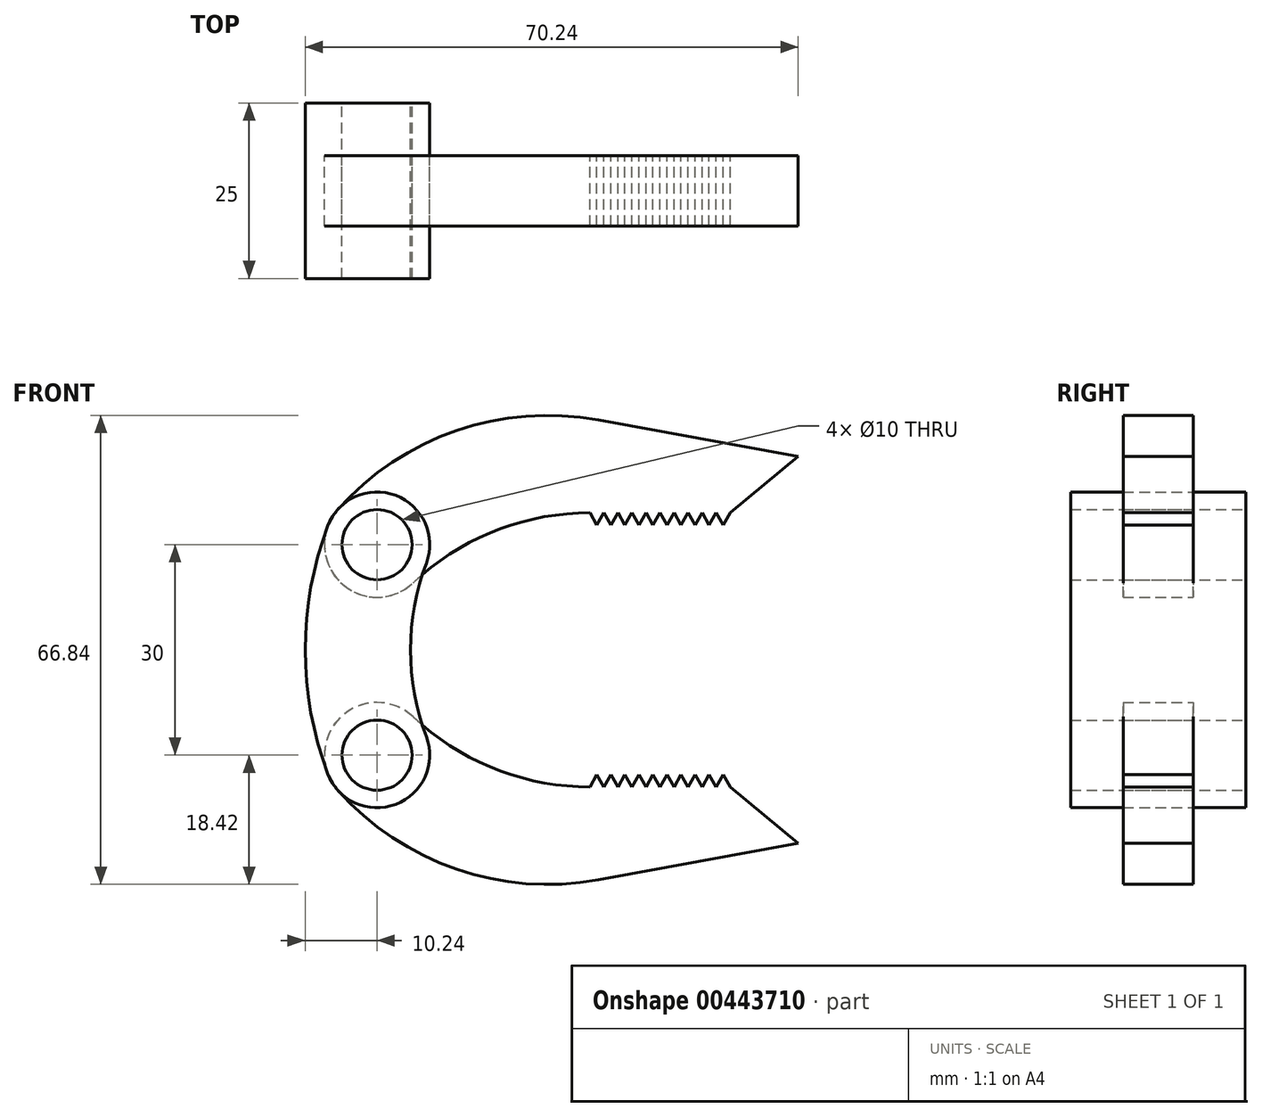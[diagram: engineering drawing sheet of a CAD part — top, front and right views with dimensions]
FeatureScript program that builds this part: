
annotation { "Feature Type Name" : "Feature", "Feature Type Description" : "" }
export const myFeature = defineFeature(function(context is Context, id is Id, definition is map)
    precondition{}
    {
        {
            var Q0;
            Q0=qCreatedBy(makeId("Front.planeOp"),FACE);
            var sketch = newSketch(context, id + "F0", { "sketchPlane" : qUnion([Q0])});
            skLineSegment(sketch, "E0", {"start": v(0, 15) * mm, "end": v(0, -15) * mm, "construction": true});
            skLineSegment(sketch, "E1", {"start": v(0, 0) * mm, "end": v(80, 0) * mm, "construction": true});
            skCircle(sketch, "E2", {"center": v(0, 15) * mm, "radius": 5 * mm});
            skCircle(sketch, "E3", {"center": v(0, -15) * mm, "radius": 5 * mm});
            skArc(sketch, "E4.0", {"start": v(7.02, 12.35) * mm, "mid": v(2.65, 22.02) * mm, "end": v(-7.02, 17.65) * mm});
            skArc(sketch, "E5.0", {"start": v(-7.02, -17.65) * mm, "mid": v(2.65, -22.02) * mm, "end": v(7.02, -12.35) * mm});
            skArc(sketch, "E6", {"start": v(-7.02, 17.65) * mm, "mid": v(-10.24, 0) * mm, "end": v(-7.02, -17.65) * mm});
            skArc(sketch, "E7", {"start": v(7.02, 12.35) * mm, "mid": v(4.76, 0) * mm, "end": v(7.02, -12.35) * mm});
            skSolve(sketch);
        }
        {
            var Q0;
            Q0=qCreatedBy(makeId("Front.planeOp"),FACE);
            var sketch = newSketch(context, id + "F1", { "sketchPlane" : qUnion([Q0])});
            skCircle(sketch, "E8.0", {"center": v(0, 15) * mm, "radius": 5 * mm});
            skArc(sketch, "E9", {"start": v(-5.6, 19.98) * mm, "mid": v(-5.22, 9.62) * mm, "end": v(5.14, 9.54) * mm});
            skCircle(sketch, "E10.0", {"center": v(0, -15) * mm, "radius": 5 * mm});
            skArc(sketch, "E11", {"start": v(5.14, -9.54) * mm, "mid": v(-5.22, -9.62) * mm, "end": v(-5.6, -19.98) * mm});
            skArc(sketch, "E12", {"start": v(31.53, 32.77) * mm, "mid": v(11.28, 31.25) * mm, "end": v(-5.6, 19.98) * mm});
            skLineSegment(sketch, "E13", {"start": v(31.53, 32.77) * mm, "end": v(60, 27.54) * mm});
            skLineSegment(sketch, "E14", {"start": v(60, 27.54) * mm, "end": v(50.33, 19.54) * mm});
            skArc(sketch, "E15", {"start": v(30.33, 19.54) * mm, "mid": v(16.78, 16.95) * mm, "end": v(5.14, 9.54) * mm});
            skLineSegment(sketch, "E16", {"start": v(19.1, 0) * mm, "end": v(64.22, 0) * mm});
            skLineSegment(sketch, "E17.MirrorCS", {"start": v(60, -27.54) * mm, "end": v(50.33, -19.54) * mm});
            skLineSegment(sketch, "E18.MirrorCS", {"start": v(31.53, -32.77) * mm, "end": v(60, -27.54) * mm});
            skArc(sketch, "E19.MirrorCS", {"start": v(30.33, -19.54) * mm, "mid": v(16.78, -16.95) * mm, "end": v(5.14, -9.54) * mm});
            skArc(sketch, "E20.MirrorCS", {"start": v(31.53, -32.77) * mm, "mid": v(11.28, -31.25) * mm, "end": v(-5.6, -19.98) * mm});
            skPoint(sketch, "E21.orphan", {"position": v(0.14, -3.73) * mm});
            skPoint(sketch, "E22.orphan", {"position": v(0.14, 3.73) * mm});
            skArc(sketch, "E23", {"start": v(16.2, 30.37) * mm, "mid": v(13.71, 28.89) * mm, "end": v(15.32, 26.48) * mm});
            skArc(sketch, "E24", {"start": v(29.56, 22.46) * mm, "mid": v(32.05, 23.95) * mm, "end": v(30.44, 26.36) * mm});
            skLineSegment(sketch, "E25", {"start": v(16.2, 30.37) * mm, "end": v(30.44, 26.37) * mm});
            skLineSegment(sketch, "E26", {"start": v(15.32, 26.48) * mm, "end": v(29.56, 22.46) * mm});
            skLineSegment(sketch, "E27.MirrorCS", {"start": v(30.1, -24.39) * mm, "end": v(15.66, -28.45) * mm, "construction": true});
            skLineSegment(sketch, "E28.MirrorCS", {"start": v(31.53, -32.77) * mm, "end": v(30.1, -24.39) * mm, "construction": true});
            skArc(sketch, "E29.MirrorC", {"start": v(29.56, -22.46) * mm, "mid": v(32.05, -23.95) * mm, "end": v(30.44, -26.36) * mm});
            skLineSegment(sketch, "E30.MirrorCS", {"start": v(15.32, -26.48) * mm, "end": v(29.56, -22.46) * mm});
            skLineSegment(sketch, "E31.MirrorCS", {"start": v(16.2, -30.37) * mm, "end": v(30.44, -26.37) * mm});
            skArc(sketch, "E32.MirrorC", {"start": v(16.2, -30.37) * mm, "mid": v(13.71, -28.89) * mm, "end": v(15.32, -26.48) * mm});
            skLineSegment(sketch, "E33", {"start": v(30.33, 19.54) * mm, "end": v(31.33, 17.8) * mm});
            skLineSegment(sketch, "E34", {"start": v(31.33, 17.8) * mm, "end": v(32.33, 19.54) * mm});
            skLineSegment(sketch, "E35", {"start": v(32.33, 19.54) * mm, "end": v(33.33, 17.8) * mm});
            skLineSegment(sketch, "E36", {"start": v(33.33, 17.8) * mm, "end": v(34.33, 19.54) * mm});
            skLineSegment(sketch, "E37", {"start": v(34.33, 19.54) * mm, "end": v(35.33, 17.8) * mm});
            skLineSegment(sketch, "E38", {"start": v(35.33, 17.8) * mm, "end": v(36.33, 19.54) * mm});
            skLineSegment(sketch, "E39", {"start": v(38.33, 19.54) * mm, "end": v(39.33, 17.8) * mm});
            skLineSegment(sketch, "E40", {"start": v(39.33, 17.8) * mm, "end": v(40.33, 19.54) * mm});
            skLineSegment(sketch, "E41", {"start": v(36.33, 19.54) * mm, "end": v(37.33, 17.8) * mm});
            skLineSegment(sketch, "E42", {"start": v(37.33, 17.8) * mm, "end": v(38.33, 19.54) * mm});
            skLineSegment(sketch, "E43", {"start": v(40.33, 19.54) * mm, "end": v(41.33, 17.8) * mm});
            skLineSegment(sketch, "E44", {"start": v(41.33, 17.8) * mm, "end": v(42.33, 19.54) * mm});
            skLineSegment(sketch, "E45", {"start": v(48.33, 19.54) * mm, "end": v(49.33, 17.8) * mm});
            skLineSegment(sketch, "E46", {"start": v(49.33, 17.8) * mm, "end": v(50.33, 19.54) * mm});
            skLineSegment(sketch, "E47", {"start": v(46.33, 19.54) * mm, "end": v(47.33, 17.8) * mm});
            skLineSegment(sketch, "E48", {"start": v(47.33, 17.8) * mm, "end": v(48.33, 19.54) * mm});
            skLineSegment(sketch, "E49", {"start": v(44.33, 19.54) * mm, "end": v(45.33, 17.8) * mm});
            skLineSegment(sketch, "E50", {"start": v(45.33, 17.8) * mm, "end": v(46.33, 19.54) * mm});
            skLineSegment(sketch, "E51", {"start": v(42.33, 19.54) * mm, "end": v(43.33, 17.8) * mm});
            skLineSegment(sketch, "E52", {"start": v(43.33, 17.8) * mm, "end": v(44.33, 19.54) * mm});
            skLineSegment(sketch, "E53.MirrorCS", {"start": v(30.33, -19.54) * mm, "end": v(31.33, -17.8) * mm});
            skLineSegment(sketch, "E54.MirrorCS", {"start": v(41.33, -17.8) * mm, "end": v(42.33, -19.54) * mm});
            skLineSegment(sketch, "E55.MirrorCS", {"start": v(48.33, -19.54) * mm, "end": v(49.33, -17.8) * mm});
            skLineSegment(sketch, "E56.MirrorCS", {"start": v(37.33, -17.8) * mm, "end": v(38.33, -19.54) * mm});
            skLineSegment(sketch, "E57.MirrorCS", {"start": v(45.33, -17.8) * mm, "end": v(46.33, -19.54) * mm});
            skLineSegment(sketch, "E58.MirrorCS", {"start": v(38.33, -19.54) * mm, "end": v(39.33, -17.8) * mm});
            skLineSegment(sketch, "E59.MirrorCS", {"start": v(47.33, -17.8) * mm, "end": v(48.33, -19.54) * mm});
            skLineSegment(sketch, "E60.MirrorCS", {"start": v(34.33, -19.54) * mm, "end": v(35.33, -17.8) * mm});
            skLineSegment(sketch, "E61.MirrorCS", {"start": v(35.33, -17.8) * mm, "end": v(36.33, -19.54) * mm});
            skLineSegment(sketch, "E62.MirrorCS", {"start": v(42.33, -19.54) * mm, "end": v(43.33, -17.8) * mm});
            skLineSegment(sketch, "E63.MirrorCS", {"start": v(46.33, -19.54) * mm, "end": v(47.33, -17.8) * mm});
            skLineSegment(sketch, "E64.MirrorCS", {"start": v(44.33, -19.54) * mm, "end": v(45.33, -17.8) * mm});
            skLineSegment(sketch, "E65.MirrorCS", {"start": v(43.33, -17.8) * mm, "end": v(44.33, -19.54) * mm});
            skLineSegment(sketch, "E66.MirrorCS", {"start": v(33.33, -17.8) * mm, "end": v(34.33, -19.54) * mm});
            skLineSegment(sketch, "E67.MirrorCS", {"start": v(31.33, -17.8) * mm, "end": v(32.33, -19.54) * mm});
            skLineSegment(sketch, "E68.MirrorCS", {"start": v(49.33, -17.8) * mm, "end": v(50.33, -19.54) * mm});
            skLineSegment(sketch, "E69.MirrorCS", {"start": v(36.33, -19.54) * mm, "end": v(37.33, -17.8) * mm});
            skLineSegment(sketch, "E70.MirrorCS", {"start": v(39.33, -17.8) * mm, "end": v(40.33, -19.54) * mm});
            skLineSegment(sketch, "E71.MirrorCS", {"start": v(32.33, -19.54) * mm, "end": v(33.33, -17.8) * mm});
            skLineSegment(sketch, "E72.MirrorCS", {"start": v(40.33, -19.54) * mm, "end": v(41.33, -17.8) * mm});
            skPoint(sketch, "E73.MirrorCS.start.orphan", {"position": v(50.33, -19.54) * mm});
            skSolve(sketch);
        }
        {
            var Q0;
            Q0 = qSketchRegion(id + "F0", true);
            extrude(context, id + "F2", {"entities" : qUnion([Q0]), "endBound" : BoundingType.SYMMETRIC, "depth" : 25 * mm});
        }
        {
            var Q0;
            Q0 = qSketchRegion(id + "F1", true);
            extrude(context, id + "F3", {"entities" : qUnion([Q0]), "endBound" : BoundingType.SYMMETRIC, "depth" : 10 * mm});
        }
    });
